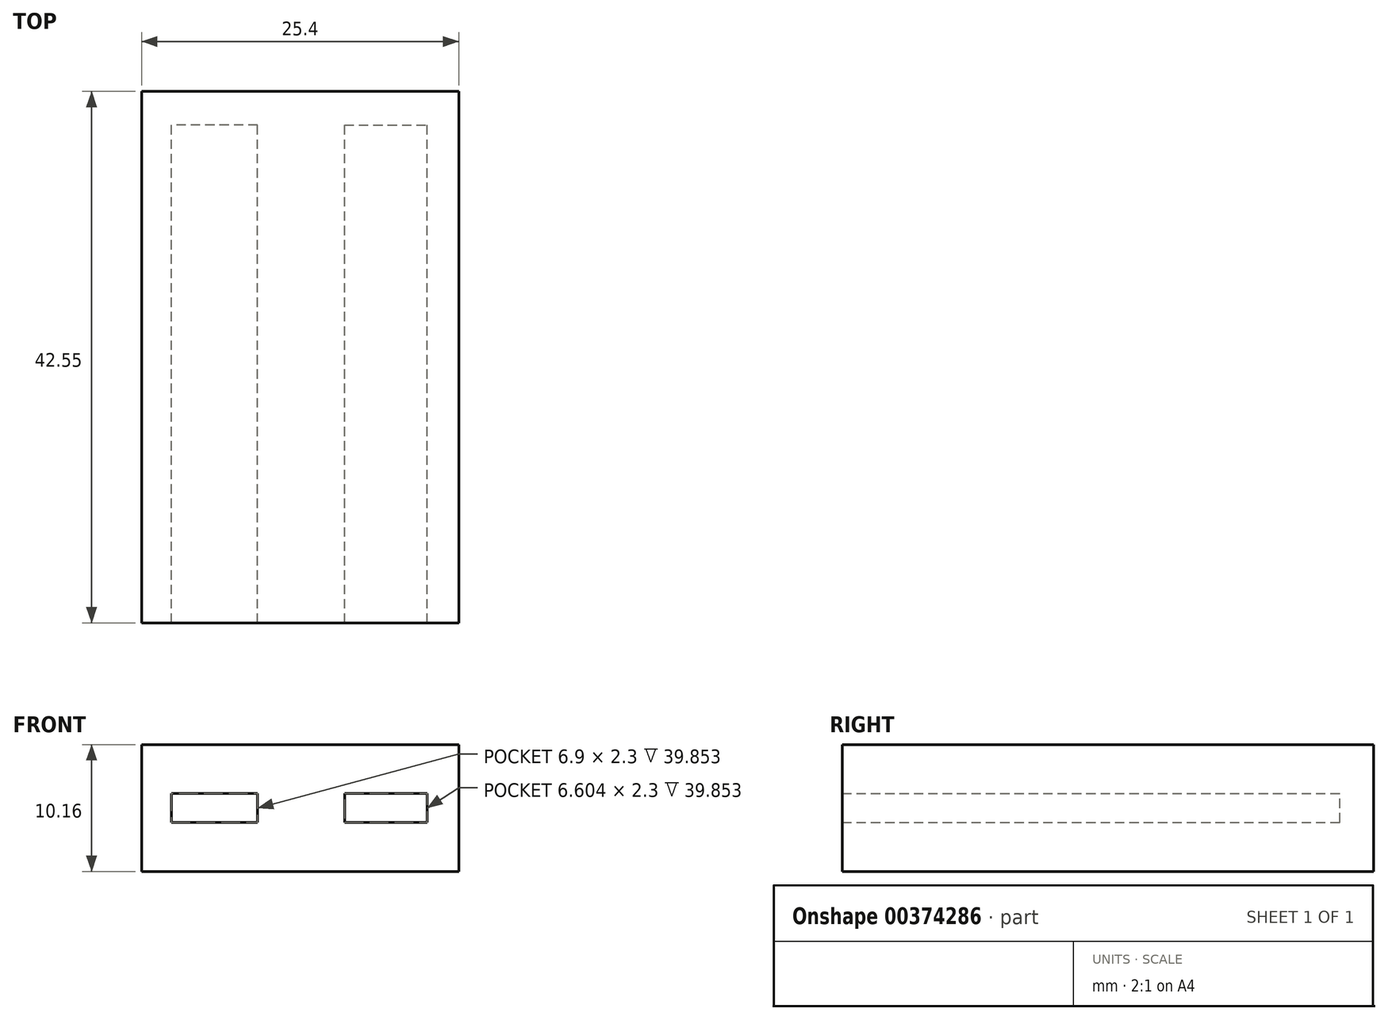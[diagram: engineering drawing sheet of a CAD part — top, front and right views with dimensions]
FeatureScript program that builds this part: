
annotation { "Feature Type Name" : "Feature", "Feature Type Description" : "" }
export const myFeature = defineFeature(function(context is Context, id is Id, definition is map)
    precondition{}
    {
        {
            var Q0;
            Q0=qCreatedBy(makeId("Front.planeOp"),FACE);
            var sketch = newSketch(context, id + "F0", { "sketchPlane" : qUnion([Q0])});
            skLineSegment(sketch, "E0.bottom", {"start": v(12.7, -5.08) * mm, "end": v(-12.7, -5.08) * mm});
            skLineSegment(sketch, "E0.top", {"start": v(12.7, 5.08) * mm, "end": v(-12.7, 5.08) * mm});
            skLineSegment(sketch, "E0.left", {"start": v(12.7, -5.08) * mm, "end": v(12.7, 5.08) * mm});
            skLineSegment(sketch, "E0.right", {"start": v(-12.7, -5.08) * mm, "end": v(-12.7, 5.08) * mm});
            skPoint(sketch, "E0.middle", {"position": v(0, 0) * mm});
            skLineSegment(sketch, "E1.bottom", {"start": v(-3.4, -1.15) * mm, "end": v(-10.3, -1.15) * mm});
            skLineSegment(sketch, "E1.top", {"start": v(-3.4, 1.15) * mm, "end": v(-10.3, 1.15) * mm});
            skLineSegment(sketch, "E1.left", {"start": v(-3.4, -1.15) * mm, "end": v(-3.4, 1.15) * mm});
            skLineSegment(sketch, "E1.right", {"start": v(-10.3, -1.15) * mm, "end": v(-10.3, 1.15) * mm});
            skPoint(sketch, "E1.middle", {"position": v(-6.86, 0) * mm});
            skPoint(sketch, "E2.middle", {"position": v(0, 12.7) * mm});
            skLineSegment(sketch, "E3.MirrorCS", {"start": v(3.56, -1.15) * mm, "end": v(3.56, 1.15) * mm});
            skLineSegment(sketch, "E4.MirrorCS", {"start": v(10.16, -1.15) * mm, "end": v(10.16, 1.15) * mm});
            skPoint(sketch, "E5.orphan", {"position": v(0, 7.6) * mm});
            skLineSegment(sketch, "E6.MirrorCS", {"start": v(3.4, 1.15) * mm, "end": v(10.3, 1.15) * mm});
            skLineSegment(sketch, "E7.MirrorCS", {"start": v(3.4, -1.15) * mm, "end": v(10.3, -1.15) * mm});
            skSolve(sketch);
        }
        {
            var Q0;
            Q0=makeQuery(id+"F0.imprint","IMPRINT",FACE,{"disambiguationData":[TD([[makeQuery(id+"F0.imprint","IMPRINT",EDGE,{"derivedFrom":sQuery(id+"F0.wireOp",EDGE,"E0.bottom")}),-1.0]])]});
            extrude(context, id + "F1", {"entities" : qUnion([Q0]), "depth" : 39.85 * mm});
        }
        {
            var Q0;
            Q0=makeQuery(id+"F0.imprint","IMPRINT",FACE,{"disambiguationData":[TD([[makeQuery(id+"F0.imprint","IMPRINT",EDGE,{"derivedFrom":sQuery(id+"F0.wireOp",EDGE,"E0.bottom")}),-1.0]])]});
            var Q1;
            Q1=makeQuery(id+"F0.imprint","IMPRINT",FACE,{"disambiguationData":[TD([[makeQuery(id+"F0.imprint","IMPRINT",EDGE,{"derivedFrom":sQuery(id+"F0.wireOp",EDGE,"E1.bottom")}),-1.0]])]});
            var Q2;
            {var subQ0=sQuery(id+"F0.wireOp",EDGE,"E3.MirrorCS");Q2=makeQuery(id+"F0.imprint","IMPRINT",FACE,{"disambiguationData":[TD([[makeQuery(id+"F0.imprint","IMPRINT",EDGE,{"derivedFrom":subQ0}),-1.0]])]});}
            extrude(context, id + "F2", {"entities" : qUnion([Q0, Q1, Q2]), "operationType" : NewBodyOperationType.ADD, "oppositeDirection" : true, "depth" : 2.7 * mm});
        }
    });
